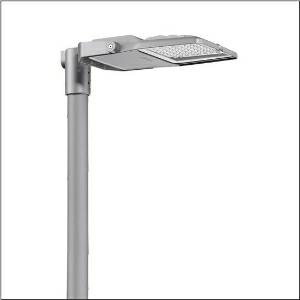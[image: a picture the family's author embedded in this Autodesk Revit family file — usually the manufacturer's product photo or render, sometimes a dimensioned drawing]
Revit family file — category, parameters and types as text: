
# Revit family: floodlight_fl_21_iq_mini___pl61_5xa7772c4c3a_2e37
name_source: partatom
category: Lighting Fixtures
units: mm (PartAtom-declared; Revit-internal decimal feet)

## family parameters
Cut with Voids When Loaded = No
Host = Face
Light Source = No
Part Type = Normal
Room Calculation Point = No
Round Connector Dimension = Use Diameter
Shared = No

## types (1)
- --- (1 x LED, 12490 lm, 87.2 W, 4000K)
    Apparent Load = 87 VA
    CIE Flux Codes = 33 65 98 100 100
    Color Rendering = 70
    Color Temperature = 4000K
    Default Elevation = 1800 mm
    Description = Floodlight FL 21 iQ mini, floodlight, primary light control with lens, of PMMA, primary optical cover: protective disc, of toughened safety glass, transparent, light distribution: PL61, light emission: direct distribution, installation type: surface-mounted, LED, High Power LED, rated luminous flux: 12.490lm, luminous efficacy: 143lm/W, light colour: 740, colour temperature: 4000K, control gear: iQ Street-Remote/DALI, control: Auto-Match, Temp-Guard, Night-Set, Smart-Wire, Desk-Remote (wireless, voltage-free reading and setting of iQ features in the workshop via application-optimized NFC function/RFID function), optimised constant luminous flux control (CLO 2.0), Light-Fading, Lumen-Switch, with terminal, 6-pole, mains connection: 220..240V, AC, 50/60Hz, start of lifetime: 87W, end of service life: 92W, reduction: 40W, luminaire housing, of diecast aluminium, powder-coated, Siteco® metallic grey (DB 702S), corrosivity category C5 mid according to DIN EN ISO 12944, suitable for swimming pools, chlorine-resistant, sealing non-destructively replaceable, please order mast flange separately, mast bracket, of steel, galvanised, powder-coated, protection rating (complete): IP66, insulation class (complete): insulation class II (safety insulation), certification: CE, ENEC, VDE, protection symbol: D, impact resistance: IK08, permissible operating ambient temperature: -40..+40°C, permissible operating ambient temperature for outdoor applications: -40..+50°C, standard: DIN EN 12944, LABS conformity tested according to VDMA 24364:2018-05, packaging unit: 1 piece

Light Distribution: PL61
    Height = 70 mm
    Lamp = 1 x LED
    Lamp Light Flux = 12490 lm
    Lamp Power = 87.2 W
    Lamp count = 1
    Length = 485 mm
    Luminous efficacy = 143 lm/W
    Manufacturer = Siteco
    ModVariant = No
    Model = 5XA7772C4C3A
    Number of Poles = 1
    OnlyDefault = Yes
    Power Factor = 1
    Product Name = Floodlight FL 21 iQ mini | PL61
    Product group = floodlight | pylon annexe
    ProductGroupID = 6200
    Protection Class = Protection class II
    Protection Degree = IP 66
    RLX_Detail_Level = 1
    RLX_Emergency_Light_Flux = 0 lm
    RLX_Emergency_Type = 0
    RLX_Emergency_Type_DB = No
    RlxData = <blob elided: 101269 chars, md5=545a903c>
    Socket = socket
    Standby Power = 0 W
    System Light Flux = 12490 lm
    System Power = 87 W
    Type Comments = factory setting: luminous flux: 100 % | dim-lin: 254 | 456 mA
    Type Image = l_1007125.jpg
    URL = http://relux.com
    VarID = @adj_172900
    Voltage = 0 V
    Weight = 0.00 kg
    Width = 337 mm

## geometry (parser evidence)
native form markers: Blend x4, Sweep x12
no freeform markers — native parametric forms only
